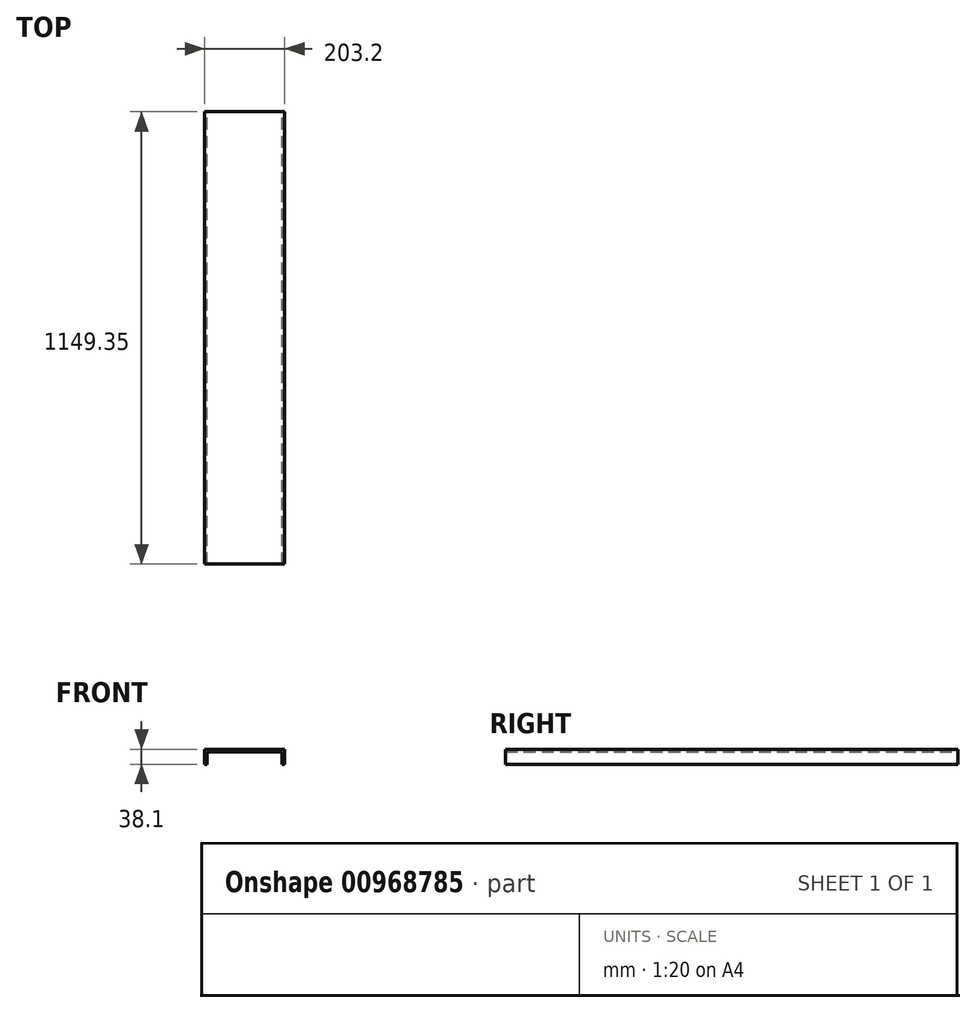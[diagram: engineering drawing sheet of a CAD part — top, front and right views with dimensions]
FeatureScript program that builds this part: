
annotation { "Feature Type Name" : "Feature", "Feature Type Description" : "" }
export const myFeature = defineFeature(function(context is Context, id is Id, definition is map)
    precondition{}
    {
        {
            var Q0;
            Q0=qCreatedBy(makeId("Front.planeOp"),FACE);
            var sketch = newSketch(context, id + "F0", { "sketchPlane" : qUnion([Q0])});
            skLineSegment(sketch, "E0.bottom", {"start": v(0, 0) * mm, "end": v(6.35, 0) * mm});
            skLineSegment(sketch, "E0.top", {"start": v(0, 38.1) * mm, "end": v(203.2, 38.1) * mm});
            skLineSegment(sketch, "E0.left", {"start": v(0, 0) * mm, "end": v(0, 38.1) * mm});
            skLineSegment(sketch, "E0.right", {"start": v(203.2, 0) * mm, "end": v(203.2, 38.1) * mm});
            skLineSegment(sketch, "E1.top", {"start": v(6.35, 31.75) * mm, "end": v(196.85, 31.75) * mm});
            skLineSegment(sketch, "E1.left", {"start": v(6.35, 0) * mm, "end": v(6.35, 31.75) * mm});
            skLineSegment(sketch, "E1.right", {"start": v(196.85, 0) * mm, "end": v(196.85, 31.75) * mm});
            skLineSegment(sketch, "E2.trimOffspring", {"start": v(196.85, 0) * mm, "end": v(203.2, 0) * mm});
            skSolve(sketch);
        }
        {
            var Q0;
            Q0 = qSketchRegion(id + "F0", true);
            extrude(context, id + "F1", {"entities" : qUnion([Q0]), "depth" : 1149.35 * mm, "offsetDistance" : 25.4 * mm});
        }
    });
